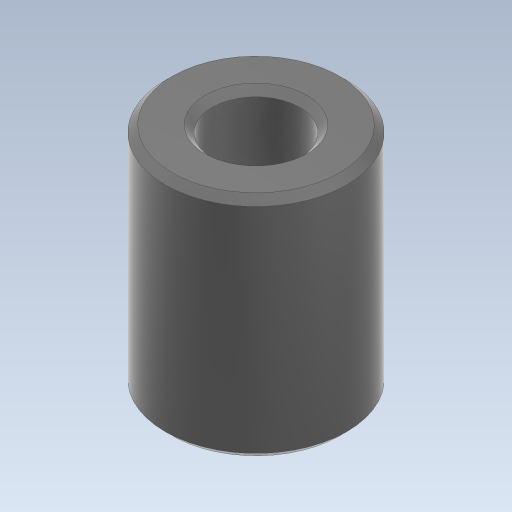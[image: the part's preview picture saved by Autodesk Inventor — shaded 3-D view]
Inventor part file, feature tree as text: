
AUTODESK INVENTOR PART (.ipt)
format: ipt  version: 2023 (Build 270158000, 158)  size: 310,784 bytes
history: native  units: mm
features: extrude x1, chamfer x1, sketch x1
ambient origin geometry x8: Origin, YZ Plane, XZ Plane, XY Plane, X Axis, Y Axis, Z Axis, Center Point
bodies: Solid1 (feature_tree)
feature tree (3):
  extrude  "Extrusion1"  Depth=13.0mm
  chamfer  "Chamfer1"  Distance=13.0mm
  sketch  "Sketch1"  dims[d0=5.0mm d1=10.35mm d2=13.0mm d3=0.0mm d4=0.4mm d5=2.0mm d6=45.0deg]
